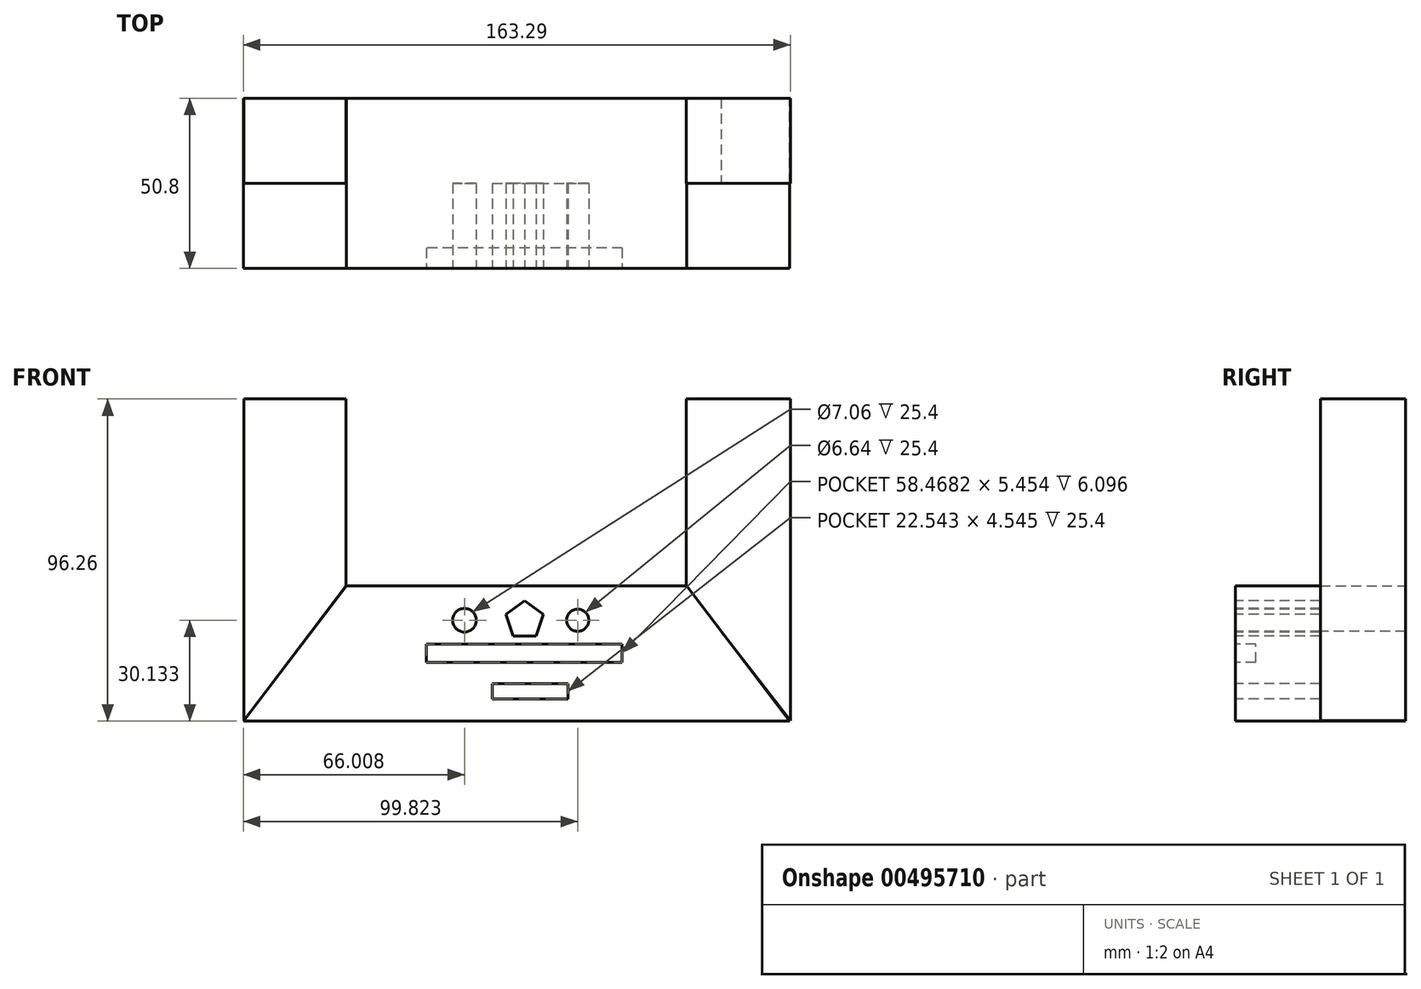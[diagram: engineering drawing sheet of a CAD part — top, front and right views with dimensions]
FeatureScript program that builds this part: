
annotation { "Feature Type Name" : "Feature", "Feature Type Description" : "" }
export const myFeature = defineFeature(function(context is Context, id is Id, definition is map)
    precondition{}
    {
        {
            var Q0;
            Q0=qCreatedBy(makeId("Front.planeOp"),FACE);
            var sketch = newSketch(context, id + "F0", { "sketchPlane" : qUnion([Q0])});
            skLineSegment(sketch, "E0", {"start": v(-53.1, 0) * mm, "end": v(48.5, 0) * mm});
            skLineSegment(sketch, "E1", {"start": v(48.5, 0) * mm, "end": v(79.25, -40.43) * mm});
            skLineSegment(sketch, "E2", {"start": v(-53.1, 0) * mm, "end": v(-83.86, -40.43) * mm});
            skLineSegment(sketch, "E3", {"start": v(-83.86, -40.43) * mm, "end": v(79.25, -40.43) * mm});
            skSolve(sketch);
        }
        {
            var Q0;
            Q0=makeQuery(id+"F0.imprint","IMPRINT",FACE,{"disambiguationData":[TD([[makeQuery(id+"F0.imprint","IMPRINT",EDGE,{"derivedFrom":sQuery(id+"F0.wireOp",EDGE,"E0")}),-1.0]])]});
            extrude(context, id + "F1", {"entities" : qUnion([Q0]), "depth" : 50.8 * mm});
        }
        {
            var Q0;
            Q0=qCreatedBy(makeId("Front.planeOp"),FACE);
            var sketch = newSketch(context, id + "F2", { "sketchPlane" : qUnion([Q0])});
            skLineSegment(sketch, "E4", {"start": v(-53.25, 0) * mm, "end": v(-53.25, 55.83) * mm});
            skLineSegment(sketch, "E5", {"start": v(-83.76, -40.3) * mm, "end": v(-83.76, 55.83) * mm});
            skLineSegment(sketch, "E6", {"start": v(-83.76, 55.83) * mm, "end": v(-53.25, 55.83) * mm});
            skLineSegment(sketch, "E7", {"start": v(48.35, 0) * mm, "end": v(48.35, 55.83) * mm});
            skLineSegment(sketch, "E8", {"start": v(79.43, -40.3) * mm, "end": v(79.43, 55.83) * mm});
            skLineSegment(sketch, "E9", {"start": v(79.43, 55.83) * mm, "end": v(48.35, 55.83) * mm});
            skLineSegment(sketch, "E10", {"start": v(-83.76, -40.3) * mm, "end": v(-53.25, 0) * mm});
            skLineSegment(sketch, "E11", {"start": v(48.35, 0) * mm, "end": v(79.43, -40.3) * mm});
            skSolve(sketch);
        }
        {
            var Q0;
            Q0 = qSketchRegion(id + "F2", true);
            extrude(context, id + "F3", {"entities" : qUnion([Q0]), "operationType" : NewBodyOperationType.ADD, "depth" : 25.4 * mm});
        }
        {
            var Q0;
            Q0=makeQuery(id+"F1.opExtrude","CAP_FACE",FACE,{"disambiguationData":[OSD([sQuery(id+"F0.wireOp",EDGE,"E0"),sQuery(id+"F0.wireOp",EDGE,"E1"),sQuery(id+"F0.wireOp",EDGE,"E2"),sQuery(id+"F0.wireOp",EDGE,"E3")])],"isStart":false});
            var sketch = newSketch(context, id + "F4", { "sketchPlane" : qUnion([Q0])});
            skLineSegment(sketch, "E12.bottom", {"start": v(29.23, -22.84) * mm, "end": v(-29.23, -22.84) * mm});
            skLineSegment(sketch, "E12.top", {"start": v(29.23, -17.39) * mm, "end": v(-29.23, -17.39) * mm});
            skLineSegment(sketch, "E12.left", {"start": v(29.23, -22.84) * mm, "end": v(29.23, -17.39) * mm});
            skLineSegment(sketch, "E12.right", {"start": v(-29.23, -22.84) * mm, "end": v(-29.23, -17.39) * mm});
            skPoint(sketch, "E12.middle", {"position": v(0, -20.11) * mm});
            skCircle(sketch, "E13", {"center": v(0, -31.93) * mm, "radius": 2.59 * mm});
            skCircle(sketch, "E14", {"center": v(-7.85, -32.11) * mm, "radius": 1.31 * mm});
            skCircle(sketch, "E15", {"center": v(6.7, -31.93) * mm, "radius": 1.32 * mm});
            skLineSegment(sketch, "E16.bottom", {"start": v(-10.4, -13.93) * mm, "end": v(-26.76, -13.93) * mm});
            skLineSegment(sketch, "E16.top", {"start": v(-10.4, -10.66) * mm, "end": v(-26.76, -10.66) * mm});
            skLineSegment(sketch, "E16.left", {"start": v(-10.4, -13.93) * mm, "end": v(-10.4, -10.66) * mm});
            skLineSegment(sketch, "E16.right", {"start": v(-26.76, -13.93) * mm, "end": v(-26.76, -10.66) * mm});
            skPoint(sketch, "E16.middle", {"position": v(-18.58, -12.3) * mm});
            skLineSegment(sketch, "E17.bottom", {"start": v(21.42, -13.93) * mm, "end": v(5.78, -13.93) * mm});
            skLineSegment(sketch, "E17.top", {"start": v(21.42, -8.48) * mm, "end": v(5.78, -8.48) * mm});
            skLineSegment(sketch, "E17.left", {"start": v(21.42, -13.93) * mm, "end": v(21.42, -8.48) * mm});
            skLineSegment(sketch, "E17.right", {"start": v(5.78, -13.93) * mm, "end": v(5.78, -8.48) * mm});
            skPoint(sketch, "E17.middle", {"position": v(13.6, -11.2) * mm});
            skLineSegment(sketch, "E18.bottom", {"start": v(19.96, -20.11) * mm, "end": v(-19.96, -20.11) * mm});
            skLineSegment(sketch, "E18.top", {"start": v(19.96, -20.11) * mm, "end": v(-19.96, -20.11) * mm});
            skLineSegment(sketch, "E18.left", {"start": v(19.96, -20.11) * mm, "end": v(19.96, -20.11) * mm});
            skLineSegment(sketch, "E18.right", {"start": v(-19.96, -20.11) * mm, "end": v(-19.96, -20.11) * mm});
            skSolve(sketch);
        }
        {
            var Q0;
            Q0=makeQuery(id+"F4.imprint","IMPRINT",FACE,{"disambiguationData":[TD([[makeQuery(id+"F4.imprint","IMPRINT",EDGE,{"derivedFrom":sQuery(id+"F4.wireOp",EDGE,"E12.bottom")}),-1.0]])]});
            extrude(context, id + "F5", {"entities" : qUnion([Q0]), "operationType" : NewBodyOperationType.REMOVE, "oppositeDirection" : true, "depth" : 6.1 * mm});
        }
        {
            var Q0;
            Q0=makeQuery(id+"F1.opExtrude","CAP_FACE",FACE,{"disambiguationData":[OSD([sQuery(id+"F0.wireOp",EDGE,"E0"),sQuery(id+"F0.wireOp",EDGE,"E1"),sQuery(id+"F0.wireOp",EDGE,"E2"),sQuery(id+"F0.wireOp",EDGE,"E3")])],"isStart":false});
            var sketch = newSketch(context, id + "F6", { "sketchPlane" : qUnion([Q0])});
            skCircle(sketch, "E19", {"center": v(0, -32.48) * mm, "radius": 4.38 * mm});
            skCircle(sketch, "E20", {"center": v(10.15, -32.11) * mm, "radius": 1.8 * mm});
            skCircle(sketch, "E21", {"center": v(-9.67, -32.3) * mm, "radius": 1.72 * mm});
            skCircle(sketch, "E22", {"center": v(0, -10.66) * mm, "radius": 3.97 * mm});
            skLineSegment(sketch, "E23.bottom", {"start": v(-14.4, -12.48) * mm, "end": v(-22.4, -12.48) * mm});
            skLineSegment(sketch, "E23.top", {"start": v(-14.4, -10.66) * mm, "end": v(-22.4, -10.66) * mm});
            skLineSegment(sketch, "E23.left", {"start": v(-14.4, -12.48) * mm, "end": v(-14.4, -10.66) * mm});
            skLineSegment(sketch, "E23.right", {"start": v(-22.4, -12.48) * mm, "end": v(-22.4, -10.66) * mm});
            skPoint(sketch, "E23.middle", {"position": v(-18.4, -11.57) * mm});
            skLineSegment(sketch, "E24.bottom", {"start": v(21.23, -12.48) * mm, "end": v(12.15, -12.48) * mm});
            skLineSegment(sketch, "E24.top", {"start": v(21.23, -10.66) * mm, "end": v(12.15, -10.66) * mm});
            skLineSegment(sketch, "E24.left", {"start": v(21.23, -12.48) * mm, "end": v(21.23, -10.66) * mm});
            skLineSegment(sketch, "E24.right", {"start": v(12.15, -12.48) * mm, "end": v(12.15, -10.66) * mm});
            skPoint(sketch, "E24.middle", {"position": v(16.7, -11.57) * mm});
            skSolve(sketch);
        }
        {
            var Q0;
            Q0 = qSketchRegion(id + "F6", true);
            extrude(context, id + "F7", {"entities" : qUnion([Q0]), "operationType" : NewBodyOperationType.ADD, "oppositeDirection" : true, "depth" : 23.1 * mm});
        }
        {
            var Q0;
            Q0=makeQuery(id+"F1.opExtrude","CAP_FACE",FACE,{"disambiguationData":[OSD([sQuery(id+"F0.wireOp",EDGE,"E0"),sQuery(id+"F0.wireOp",EDGE,"E1"),sQuery(id+"F0.wireOp",EDGE,"E2"),sQuery(id+"F0.wireOp",EDGE,"E3")])],"isStart":false});
            var sketch = newSketch(context, id + "F8", { "sketchPlane" : qUnion([Q0])});
            skCircle(sketch, "E25.cCircle", {"center": v(0.15, -10.3) * mm, "radius": 4.73 * mm, "construction": true});
            skLineSegment(sketch, "E25.0", {"start": v(3.58, -15.02) * mm, "end": v(-3.29, -15.02) * mm});
            skLineSegment(sketch, "E25.1", {"start": v(-3.29, -15.02) * mm, "end": v(-5.41, -8.5) * mm});
            skLineSegment(sketch, "E25.2", {"start": v(-5.41, -8.5) * mm, "end": v(0.15, -4.45) * mm});
            skLineSegment(sketch, "E25.3", {"start": v(0.15, -4.45) * mm, "end": v(5.7, -8.5) * mm});
            skLineSegment(sketch, "E25.4", {"start": v(5.7, -8.5) * mm, "end": v(3.58, -15.02) * mm});
            skPoint(sketch, "E25.0.midPoint", {"position": v(0.15, -15.02) * mm});
            skCircle(sketch, "E26", {"center": v(-17.85, -10.3) * mm, "radius": 3.53 * mm});
            skCircle(sketch, "E27", {"center": v(15.96, -10.3) * mm, "radius": 3.32 * mm});
            skLineSegment(sketch, "E28.bottom", {"start": v(-9.49, -29.2) * mm, "end": v(13.05, -29.2) * mm});
            skLineSegment(sketch, "E28.top", {"start": v(-9.49, -33.75) * mm, "end": v(13.05, -33.75) * mm});
            skLineSegment(sketch, "E28.left", {"start": v(-9.49, -29.2) * mm, "end": v(-9.49, -33.75) * mm});
            skLineSegment(sketch, "E28.right", {"start": v(13.05, -29.2) * mm, "end": v(13.05, -33.75) * mm});
            skSolve(sketch);
        }
        {
            var Q0;
            Q0 = qSketchRegion(id + "F8", true);
            extrude(context, id + "F9", {"entities" : qUnion([Q0]), "operationType" : NewBodyOperationType.REMOVE, "oppositeDirection" : true, "depth" : 25.4 * mm});
        }
    });
